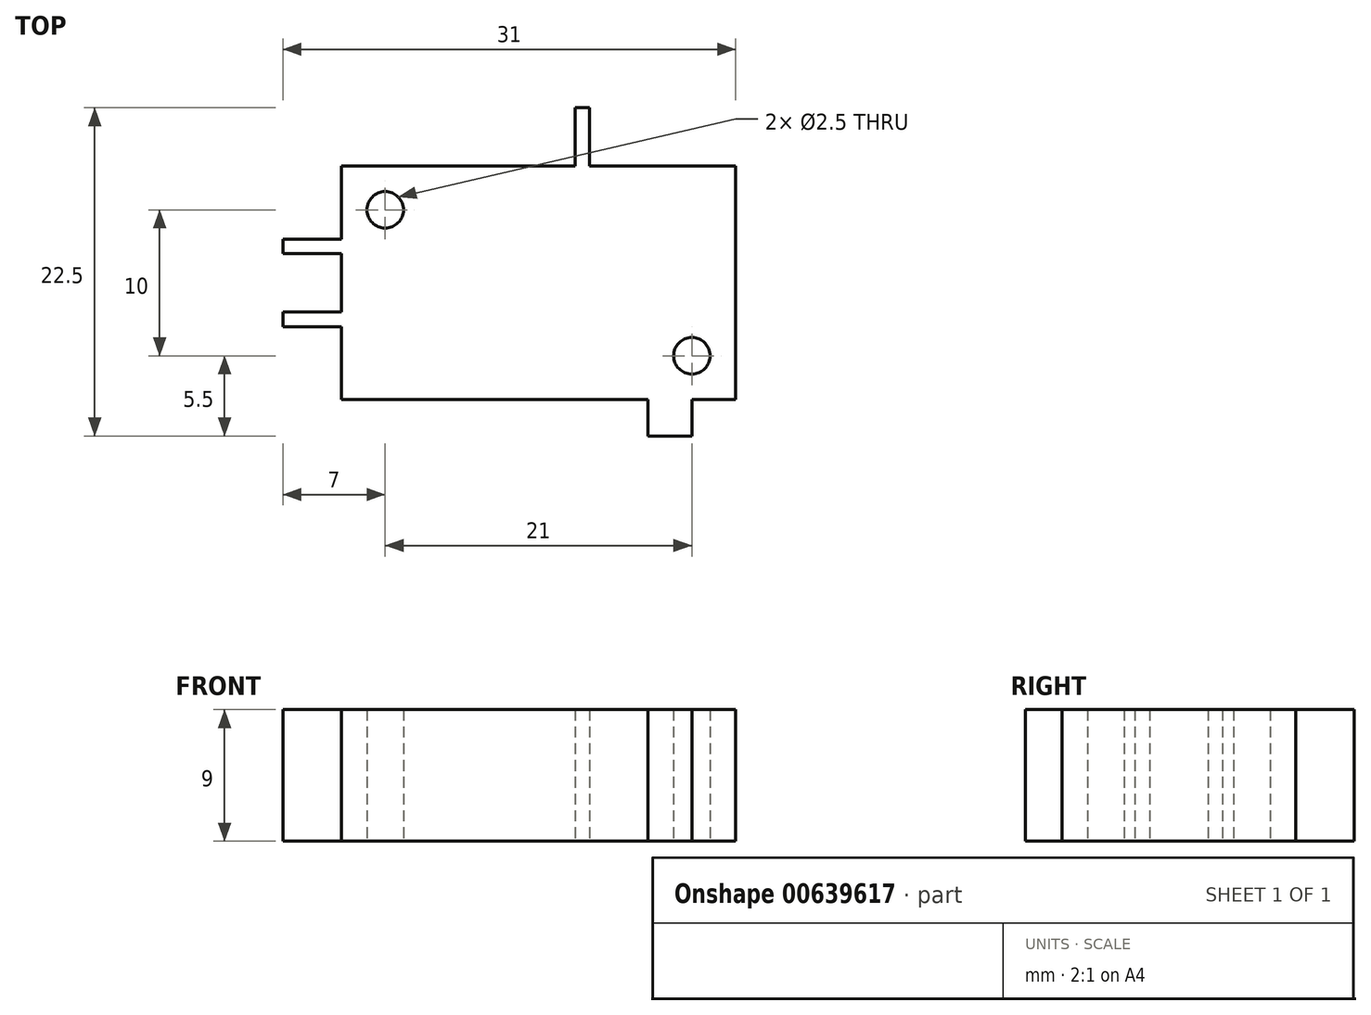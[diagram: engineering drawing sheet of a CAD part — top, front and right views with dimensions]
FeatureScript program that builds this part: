
annotation { "Feature Type Name" : "Feature", "Feature Type Description" : "" }
export const myFeature = defineFeature(function(context is Context, id is Id, definition is map)
    precondition{}
    {
        {
            var Q0;
            Q0=qCreatedBy(makeId("Top.planeOp"),FACE);
            var sketch = newSketch(context, id + "F0", { "sketchPlane" : qUnion([Q0])});
            skLineSegment(sketch, "E0.bottom", {"start": v(0, 0) * mm, "end": v(27, 0) * mm});
            skLineSegment(sketch, "E0.top", {"start": v(0, 16) * mm, "end": v(27, 16) * mm});
            skLineSegment(sketch, "E0.left", {"start": v(0, 0) * mm, "end": v(0, 16) * mm});
            skLineSegment(sketch, "E0.right", {"start": v(27, 0) * mm, "end": v(27, 16) * mm});
            skLineSegment(sketch, "E1", {"start": v(21, 0) * mm, "end": v(21, -2.5) * mm});
            skLineSegment(sketch, "E2", {"start": v(21, -2.5) * mm, "end": v(24, -2.5) * mm});
            skLineSegment(sketch, "E3", {"start": v(24, -2.5) * mm, "end": v(24, 0) * mm});
            skLineSegment(sketch, "E4", {"start": v(16, 16) * mm, "end": v(16, 20) * mm});
            skLineSegment(sketch, "E5", {"start": v(16, 20) * mm, "end": v(17, 20) * mm});
            skLineSegment(sketch, "E6", {"start": v(17, 20) * mm, "end": v(17, 16) * mm});
            skLineSegment(sketch, "E7", {"start": v(0, 11) * mm, "end": v(-4, 11) * mm});
            skLineSegment(sketch, "E8", {"start": v(-4, 11) * mm, "end": v(-4, 10) * mm});
            skLineSegment(sketch, "E9", {"start": v(-4, 10) * mm, "end": v(0, 10) * mm});
            skLineSegment(sketch, "E10", {"start": v(0, 6) * mm, "end": v(-4, 6) * mm});
            skLineSegment(sketch, "E11", {"start": v(-4, 6) * mm, "end": v(-4, 5) * mm});
            skLineSegment(sketch, "E12", {"start": v(-4, 5) * mm, "end": v(0, 5) * mm});
            skCircle(sketch, "E13", {"center": v(3, 13) * mm, "radius": 1.25 * mm});
            skCircle(sketch, "E14", {"center": v(24, 3) * mm, "radius": 1.25 * mm});
            skSolve(sketch);
        }
        {
            var Q0;
            {var subQ7=sQuery(id+"F0.wireOp",EDGE,"E0.right");Q0=makeQuery(id+"F0.imprint","IMPRINT",FACE,{"disambiguationData":[TD([[makeQuery(id+"F0.imprint","IMPRINT",EDGE,{"derivedFrom":subQ7}),1.0]])]});}
            var Q1;
            {var subQ0=sQuery(id+"F0.wireOp",EDGE,"E10");Q1=makeQuery(id+"F0.imprint","IMPRINT",FACE,{"disambiguationData":[TD([[makeQuery(id+"F0.imprint","IMPRINT",EDGE,{"derivedFrom":subQ0}),1.0]])]});}
            var Q2;
            {var subQ0=sQuery(id+"F0.wireOp",EDGE,"E7");Q2=makeQuery(id+"F0.imprint","IMPRINT",FACE,{"disambiguationData":[TD([[makeQuery(id+"F0.imprint","IMPRINT",EDGE,{"derivedFrom":subQ0}),1.0]])]});}
            var Q3;
            {var subQ0=sQuery(id+"F0.wireOp",EDGE,"E4");Q3=makeQuery(id+"F0.imprint","IMPRINT",FACE,{"disambiguationData":[TD([[makeQuery(id+"F0.imprint","IMPRINT",EDGE,{"derivedFrom":subQ0}),-1.0]])]});}
            var Q4;
            {var subQ0=sQuery(id+"F0.wireOp",EDGE,"E1");Q4=makeQuery(id+"F0.imprint","IMPRINT",FACE,{"disambiguationData":[TD([[makeQuery(id+"F0.imprint","IMPRINT",EDGE,{"derivedFrom":subQ0}),1.0]])]});}
            extrude(context, id + "F1", {"entities" : qUnion([Q0, Q1, Q2, Q3, Q4]), "depth" : 9 * mm, "offsetDistance" : 25 * mm});
        }
    });
